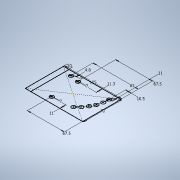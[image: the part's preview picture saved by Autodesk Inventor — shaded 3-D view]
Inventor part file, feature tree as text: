
AUTODESK INVENTOR PART (.ipt)
format: ipt  version: 2020 (Build 240168000, 168)  size: 104,960 bytes
history: native  units: mm
features: sketch x1
ambient origin geometry x8: Origin, YZ Plane, XZ Plane, XY Plane, X Axis, Y Axis, Z Axis, Center Point
feature tree (1):
  sketch  "Sketch1"  dims[d0=105.0mm d1=70.0mm d2=7.0mm d3=4.8mm d4=83.0mm d5=7.0mm d7=11.3mm d8=67.5mm d9=7.0mm d10=11.0mm d11=67.5mm d12=7.0mm d13=10.5mm d14=11.0mm d18=60.0mm d20=8.901179mm d22=10.0mm]
